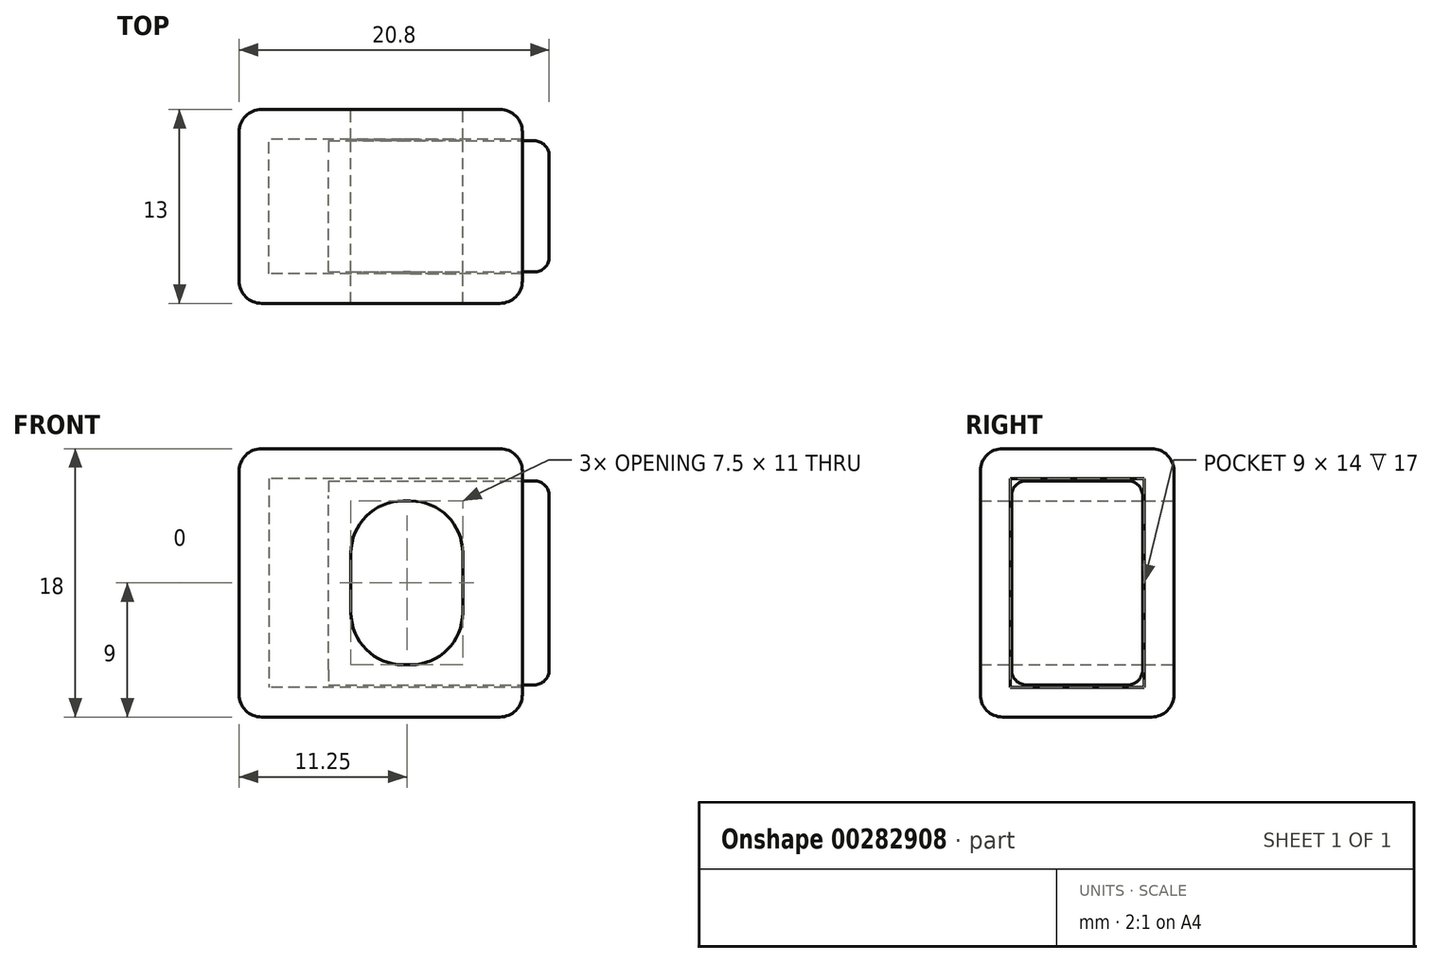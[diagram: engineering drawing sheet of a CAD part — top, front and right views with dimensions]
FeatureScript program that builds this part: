
annotation { "Feature Type Name" : "Feature", "Feature Type Description" : "" }
export const myFeature = defineFeature(function(context is Context, id is Id, definition is map)
    precondition{}
    {
        {
            var Q0;
            Q0=qCreatedBy(makeId("Front.planeOp"),FACE);
            var sketch = newSketch(context, id + "F0", { "sketchPlane" : qUnion([Q0])});
            skLineSegment(sketch, "E0.bottom", {"start": v(9.5, 9) * mm, "end": v(-9.5, 9) * mm});
            skLineSegment(sketch, "E0.top", {"start": v(9.5, -9) * mm, "end": v(-9.5, -9) * mm});
            skLineSegment(sketch, "E0.left", {"start": v(9.5, 9) * mm, "end": v(9.5, -9) * mm});
            skLineSegment(sketch, "E0.right", {"start": v(-9.5, 9) * mm, "end": v(-9.5, -9) * mm});
            skPoint(sketch, "E0.middle", {"position": v(0, 0) * mm});
            skSolve(sketch);
        }
        {
            var Q0;
            Q0=makeQuery(id+"F0.imprint","IMPRINT",FACE,{"disambiguationData":[TD([[makeQuery(id+"F0.imprint","IMPRINT",EDGE,{"derivedFrom":sQuery(id+"F0.wireOp",EDGE,"E0.bottom")}),1.0]])]});
            extrude(context, id + "F1", {"entities" : qUnion([Q0]), "endBound" : BoundingType.SYMMETRIC, "depth" : 13 * mm});
        }
        {
            var Q0;
            Q0=makeQuery(id+"F1.opExtrude","SWEPT_FACE",FACE,{"disambiguationData":[OSD([sQuery(id+"F0.wireOp",EDGE,"E0.left")])]});
            shell(context, id + "F2", {"entities" : qUnion([Q0]), "thickness" : 2 * mm});
        }
        {
            var Q0;
            Q0=makeQuery(id+"F1.opExtrude","CAP_EDGE",EDGE,{"disambiguationData":[OSD([sQuery(id+"F0.wireOp",EDGE,"E0.bottom")])],"isStart":true});
            var Q1;
            Q1=makeQuery(id+"F1.opExtrude","CAP_EDGE",EDGE,{"disambiguationData":[OSD([sQuery(id+"F0.wireOp",EDGE,"E0.top")])],"isStart":true});
            var Q2;
            Q2=makeQuery(id+"F1.opExtrude","CAP_EDGE",EDGE,{"disambiguationData":[OSD([sQuery(id+"F0.wireOp",EDGE,"E0.bottom")])],"isStart":false});
            var Q3;
            Q3=makeQuery(id+"F1.opExtrude","CAP_EDGE",EDGE,{"disambiguationData":[OSD([sQuery(id+"F0.wireOp",EDGE,"E0.top")])],"isStart":false});
            var Q4;
            Q4=makeQuery(id+"F1.opExtrude","CAP_EDGE",EDGE,{"disambiguationData":[OSD([sQuery(id+"F0.wireOp",EDGE,"E0.left")])],"isStart":false});
            var Q5;
            Q5=makeQuery(id+"F1.opExtrude","CAP_EDGE",EDGE,{"disambiguationData":[OSD([sQuery(id+"F0.wireOp",EDGE,"E0.left")])],"isStart":true});
            var Q6;
            Q6=makeQuery(id+"F1.opExtrude","SWEPT_EDGE",EDGE,{"disambiguationData":[OSD([sQuery(id+"F0.wireOp",EDGE,"E0.bottom"),sQuery(id+"F0.wireOp",EDGE,"E0.right")])]});
            var Q7;
            Q7=makeQuery(id+"F1.opExtrude","SWEPT_EDGE",EDGE,{"disambiguationData":[OSD([sQuery(id+"F0.wireOp",EDGE,"E0.bottom"),sQuery(id+"F0.wireOp",EDGE,"E0.left")])]});
            var Q8;
            Q8=makeQuery(id+"F1.opExtrude","SWEPT_EDGE",EDGE,{"disambiguationData":[OSD([sQuery(id+"F0.wireOp",EDGE,"E0.top"),sQuery(id+"F0.wireOp",EDGE,"E0.left")])]});
            var Q9;
            Q9=makeQuery(id+"F1.opExtrude","SWEPT_EDGE",EDGE,{"disambiguationData":[OSD([sQuery(id+"F0.wireOp",EDGE,"E0.top"),sQuery(id+"F0.wireOp",EDGE,"E0.right")])]});
            var Q10;
            Q10=makeQuery(id+"F1.opExtrude","CAP_EDGE",EDGE,{"disambiguationData":[OSD([sQuery(id+"F0.wireOp",EDGE,"E0.right")])],"isStart":true});
            var Q11;
            Q11=makeQuery(id+"F1.opExtrude","CAP_EDGE",EDGE,{"disambiguationData":[OSD([sQuery(id+"F0.wireOp",EDGE,"E0.right")])],"isStart":false});
            fillet(context, id + "F3", {"entities" : qUnion([Q0, Q1, Q2, Q3, Q4, Q5, Q6, Q7, Q8, Q9, Q10, Q11]), "radius" : 1.5 * mm, "tangentPropagation" : true, "allowEdgeOverflow" : false});
        }
        {
            var Q0;
            Q0=qCreatedBy(makeId("Right.planeOp"),FACE);
            cPlane(context, id + "F4", {"entities" : qUnion([Q0]), "cplaneType" : CPlaneType.OFFSET, "offset" : 11.3 * mm, "width" : 150 * mm, "height" : 150 * mm});
        }
        {
            var Q0;
            Q0=qCreatedBy(id+"F4.planeOp",FACE);
            var sketch = newSketch(context, id + "F5", { "sketchPlane" : qUnion([Q0])});
            skLineSegment(sketch, "E1.0.0", {"start": v(4.4, -6.84) * mm, "end": v(4.4, 6.84) * mm});
            skLineSegment(sketch, "E1.0.1", {"start": v(4.4, 6.84) * mm, "end": v(-4.4, 6.84) * mm});
            skLineSegment(sketch, "E1.0.2", {"start": v(-4.4, 6.84) * mm, "end": v(-4.4, -6.84) * mm});
            skLineSegment(sketch, "E1.0.3", {"start": v(-4.4, -6.84) * mm, "end": v(4.4, -6.84) * mm});
            skSolve(sketch);
        }
        {
            var Q0;
            Q0=makeQuery(id+"F5.imprint","IMPRINT",FACE,{"disambiguationData":[TD([[makeQuery(id+"F5.imprint","IMPRINT",EDGE,{"derivedFrom":sQuery(id+"F5.wireOp",EDGE,"E1.0.0")}),1.0]])]});
            extrude(context, id + "F6", {"entities" : qUnion([Q0]), "oppositeDirection" : true, "depth" : 14.8 * mm});
        }
        {
            var Q0;
            Q0=qCreatedBy(makeId("Front.planeOp"),FACE);
            var sketch = newSketch(context, id + "F7", { "sketchPlane" : qUnion([Q0])});
            skLineSegment(sketch, "E2.bottom", {"start": v(1.5, 5.5) * mm, "end": v(2, 5.5) * mm});
            skLineSegment(sketch, "E2.top", {"start": v(1.5, -5.5) * mm, "end": v(2, -5.5) * mm});
            skLineSegment(sketch, "E2.left", {"start": v(-2, 2) * mm, "end": v(-2, -2) * mm});
            skLineSegment(sketch, "E2.right", {"start": v(5.5, 2) * mm, "end": v(5.5, -2) * mm});
            skPoint(sketch, "E2.middle", {"position": v(1.75, 0) * mm});
            skPoint(sketch, "E3.visualSharp", {"position": v(-2, -5.5) * mm});
            skArc(sketch, "E3.filletArc", {"start": v(-2, -2) * mm, "mid": v(-0.97, -4.47) * mm, "end": v(1.5, -5.5) * mm});
            skPoint(sketch, "E4.visualSharp", {"position": v(5.5, -5.5) * mm});
            skArc(sketch, "E4.filletArc", {"start": v(2, -5.5) * mm, "mid": v(4.47, -4.47) * mm, "end": v(5.5, -2) * mm});
            skPoint(sketch, "E5.visualSharp", {"position": v(5.5, 5.5) * mm});
            skArc(sketch, "E5.filletArc", {"start": v(5.5, 2) * mm, "mid": v(4.47, 4.47) * mm, "end": v(2, 5.5) * mm});
            skPoint(sketch, "E6.visualSharp", {"position": v(-2, 5.5) * mm});
            skArc(sketch, "E6.filletArc", {"start": v(1.5, 5.5) * mm, "mid": v(-0.97, 4.47) * mm, "end": v(-2, 2) * mm});
            skSolve(sketch);
        }
        {
            var Q0;
            Q0=makeQuery(id+"F6.opExtrude","CAP_EDGE",EDGE,{"disambiguationData":[OSD([sQuery(id+"F5.wireOp",EDGE,"E1.0.0")])],"isStart":true});
            var Q1;
            Q1=makeQuery(id+"F6.opExtrude","CAP_EDGE",EDGE,{"disambiguationData":[OSD([sQuery(id+"F5.wireOp",EDGE,"E1.0.3")])],"isStart":true});
            var Q2;
            Q2=makeQuery(id+"F6.opExtrude","CAP_EDGE",EDGE,{"disambiguationData":[OSD([sQuery(id+"F5.wireOp",EDGE,"E1.0.2")])],"isStart":true});
            var Q3;
            Q3=makeQuery(id+"F6.opExtrude","CAP_EDGE",EDGE,{"disambiguationData":[OSD([sQuery(id+"F5.wireOp",EDGE,"E1.0.1")])],"isStart":true});
            var Q4;
            Q4=makeQuery(id+"F6.opExtrude","SWEPT_EDGE",EDGE,{"disambiguationData":[OSD([sQuery(id+"F5.wireOp",EDGE,"E1.0.0"),sQuery(id+"F5.wireOp",EDGE,"E1.0.3")])]});
            var Q5;
            Q5=makeQuery(id+"F6.opExtrude","SWEPT_EDGE",EDGE,{"disambiguationData":[OSD([sQuery(id+"F5.wireOp",EDGE,"E1.0.0"),sQuery(id+"F5.wireOp",EDGE,"E1.0.1")])]});
            var Q6;
            Q6=makeQuery(id+"F6.opExtrude","SWEPT_EDGE",EDGE,{"disambiguationData":[OSD([sQuery(id+"F5.wireOp",EDGE,"E1.0.1"),sQuery(id+"F5.wireOp",EDGE,"E1.0.2")])]});
            var Q7;
            Q7=makeQuery(id+"F6.opExtrude","SWEPT_EDGE",EDGE,{"disambiguationData":[OSD([sQuery(id+"F5.wireOp",EDGE,"E1.0.2"),sQuery(id+"F5.wireOp",EDGE,"E1.0.3")])]});
            fillet(context, id + "F8", {"entities" : qUnion([Q0, Q1, Q2, Q3, Q4, Q5, Q6, Q7]), "radius" : 1 * mm, "tangentPropagation" : true, "allowEdgeOverflow" : false});
        }
        {
            var Q0;
            Q0 = qSketchRegion(id + "F7", true);
            extrude(context, id + "F9", {"entities" : qUnion([Q0]), "operationType" : NewBodyOperationType.REMOVE, "endBound" : BoundingType.SYMMETRIC, "depth" : 25 * mm});
        }
    });
